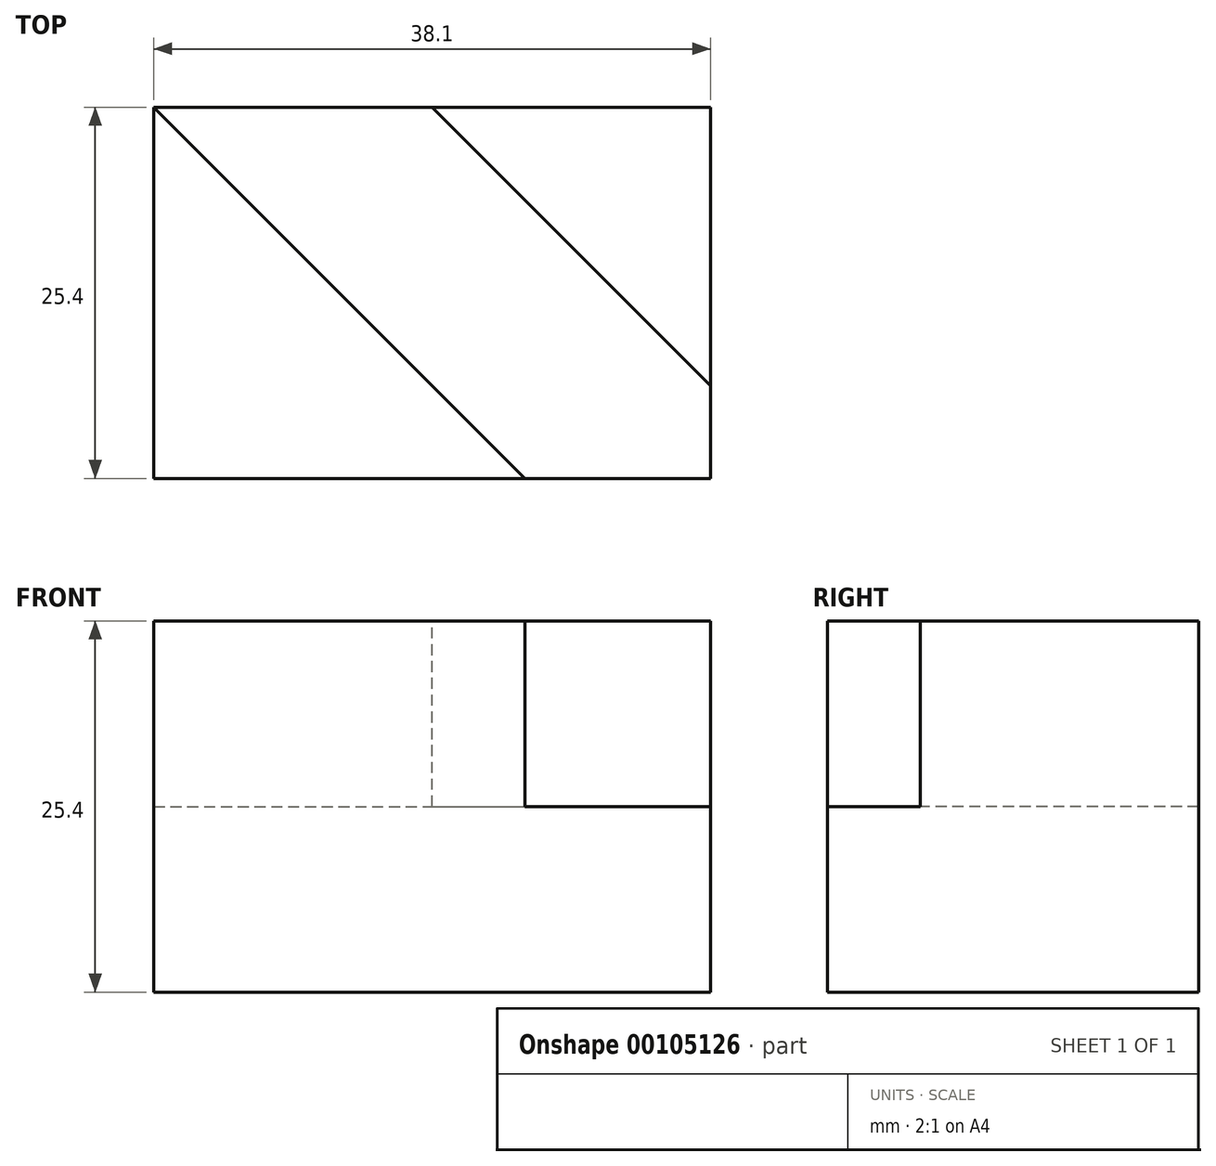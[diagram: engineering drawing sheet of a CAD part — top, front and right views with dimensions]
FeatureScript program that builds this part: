
annotation { "Feature Type Name" : "Feature", "Feature Type Description" : "" }
export const myFeature = defineFeature(function(context is Context, id is Id, definition is map)
    precondition{}
    {
        {
            var Q0;
            Q0=qCreatedBy(makeId("Front.planeOp"),FACE);
            var sketch = newSketch(context, id + "F0", { "sketchPlane" : qUnion([Q0])});
            skLineSegment(sketch, "E0", {"start": v(0, 0) * mm, "end": v(0, 25.4) * mm});
            skLineSegment(sketch, "E1", {"start": v(0, 25.4) * mm, "end": v(38.1, 25.4) * mm});
            skLineSegment(sketch, "E2", {"start": v(38.1, 25.4) * mm, "end": v(38.1, 0) * mm});
            skLineSegment(sketch, "E3", {"start": v(38.1, 0) * mm, "end": v(0, 0) * mm});
            skSolve(sketch);
        }
        {
            var Q0;
            Q0 = qSketchRegion(id + "F0", true);
            extrude(context, id + "F1", {"entities" : qUnion([Q0]), "oppositeDirection" : true, "depth" : 25.4 * mm});
        }
        {
            var Q0;
            Q0=makeQuery(id+"F1.opExtrude","SWEPT_FACE",FACE,{"disambiguationData":[OSD([sQuery(id+"F0.wireOp",EDGE,"E1")])]});
            var sketch = newSketch(context, id + "F2", { "sketchPlane" : qUnion([Q0])});
            skLineSegment(sketch, "E4", {"start": v(0, 25.4) * mm, "end": v(25.4, 0) * mm});
            skLineSegment(sketch, "E5", {"start": v(19.05, 25.4) * mm, "end": v(38.1, 6.35) * mm});
            skSolve(sketch);
        }
        {
            var Q0;
            {var subQ4=sQuery(id+"F2.wireOp",EDGE,"E4");Q0=makeQuery(id+"F2.imprint","IMPRINT",FACE,{"disambiguationData":[TD([[makeQuery(id+"F2.imprint","IMPRINT",EDGE,{"derivedFrom":subQ4}),1.0]])]});}
            extrude(context, id + "F3", {"entities" : qUnion([Q0]), "operationType" : NewBodyOperationType.REMOVE, "oppositeDirection" : true, "depth" : 12.7 * mm});
        }
    });
